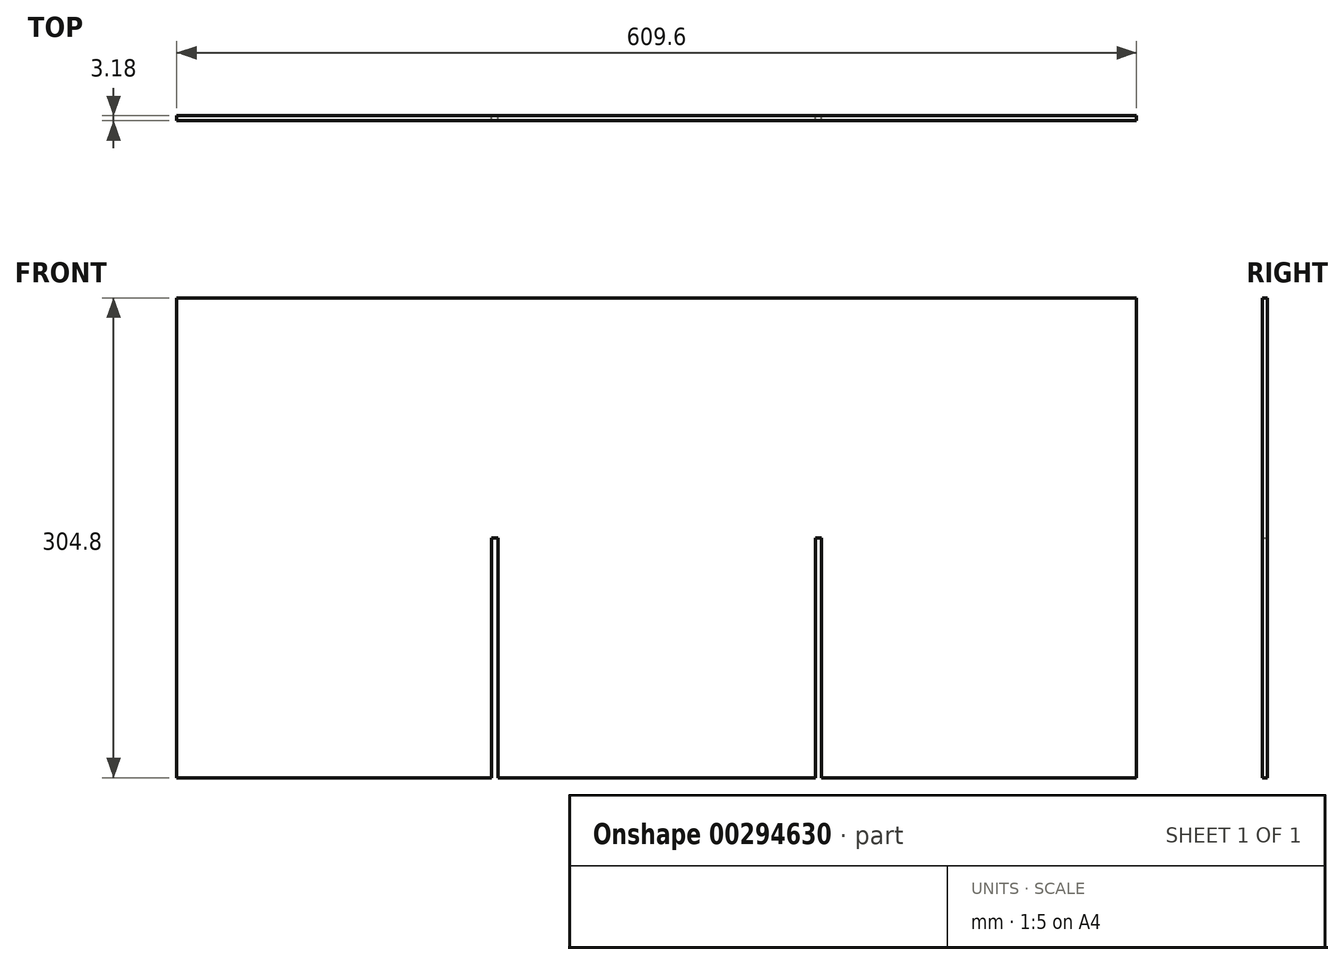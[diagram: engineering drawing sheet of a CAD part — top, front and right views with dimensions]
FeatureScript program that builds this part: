
annotation { "Feature Type Name" : "Feature", "Feature Type Description" : "" }
export const myFeature = defineFeature(function(context is Context, id is Id, definition is map)
    precondition{}
    {
        {
            var Q0;
            Q0=qCreatedBy(makeId("Front.planeOp"),FACE);
            var sketch = newSketch(context, id + "F0", { "sketchPlane" : qUnion([Q0])});
            skLineSegment(sketch, "E0.bottom", {"start": v(-310.6, 45.05) * mm, "end": v(299, 45.05) * mm});
            skLineSegment(sketch, "E0.top", {"start": v(-310.6, -259.75) * mm, "end": v(299, -259.75) * mm});
            skLineSegment(sketch, "E0.left", {"start": v(-310.6, 45.05) * mm, "end": v(-310.6, -259.75) * mm});
            skLineSegment(sketch, "E0.right", {"start": v(299, 45.05) * mm, "end": v(299, -259.75) * mm});
            skSolve(sketch);
        }
        {
            var Q0;
            Q0=qSketchRegion(id+"F0",true);
            extrude(context, id + "F1", {"entities" : qUnion([Q0]), "endBound" : BoundingType.SYMMETRIC, "depth" : 3.17 * mm});
        }
        {
            var Q0;
            Q0=makeQuery(id+"F1.opExtrude","SWEPT_FACE",FACE,{"disambiguationData":[OSD([sQuery(id+"F0.wireOp",EDGE,"E0.top")])]});
            var sketch = newSketch(context, id + "F2", { "sketchPlane" : qUnion([Q0])});
            skLineSegment(sketch, "E1.bottom", {"start": v(95, 1.59) * mm, "end": v(98.97, 1.59) * mm});
            skLineSegment(sketch, "E1.top", {"start": v(95, -1.59) * mm, "end": v(98.97, -1.59) * mm});
            skLineSegment(sketch, "E1.left", {"start": v(95, 1.59) * mm, "end": v(95, -1.59) * mm});
            skLineSegment(sketch, "E1.right", {"start": v(98.97, 1.59) * mm, "end": v(98.97, -1.59) * mm});
            skSolve(sketch);
        }
        {
            var Q0;
            Q0=qSketchRegion(id+"F2",true);
            extrude(context, id + "F3", {"entities" : qUnion([Q0]), "operationType" : NewBodyOperationType.REMOVE, "oppositeDirection" : true, "depth" : 152.4 * mm});
        }
        {
            var Q0;
            {var subQ1=sQuery(id+"F0.wireOp",EDGE,"E0.left");var subQ2=sQuery(id+"F0.wireOp",EDGE,"E0.top");Q0=makeQuery(id+"F3.boolean.opBoolean","SPLIT",FACE,{"disambiguationData":[TD([makeQuery(id+"F1.opExtrude","SWEPT_FACE",FACE,{"disambiguationData":[OSD([subQ1])]})])],"derivedFrom":makeQuery(id+"F1.opExtrude","SWEPT_FACE",FACE,{"disambiguationData":[OSD([subQ2])]})});}
            var sketch = newSketch(context, id + "F4", { "sketchPlane" : qUnion([Q0])});
            skLineSegment(sketch, "E2.bottom", {"start": v(-110.58, 1.59) * mm, "end": v(-106.6, 1.59) * mm});
            skLineSegment(sketch, "E2.top", {"start": v(-110.58, -1.59) * mm, "end": v(-106.6, -1.59) * mm});
            skLineSegment(sketch, "E2.left", {"start": v(-110.58, 1.59) * mm, "end": v(-110.58, -1.59) * mm});
            skLineSegment(sketch, "E2.right", {"start": v(-106.6, 1.59) * mm, "end": v(-106.6, -1.59) * mm});
            skSolve(sketch);
        }
        {
            var Q0;
            Q0=qSketchRegion(id+"F4",true);
            extrude(context, id + "F5", {"entities" : qUnion([Q0]), "operationType" : NewBodyOperationType.REMOVE, "oppositeDirection" : true, "depth" : 152.4 * mm});
        }
    });
